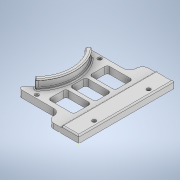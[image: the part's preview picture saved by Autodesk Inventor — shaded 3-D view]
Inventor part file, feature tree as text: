
AUTODESK INVENTOR PART (.ipt)
format: ipt  version: 2022 (Build 260153000, 153)  size: 4,516,864 bytes
history: native  units: in
note: dims shown in document units (in); Inventor stores cm internally (conversion verified against a paired STEP export)
features: sketch x19, extrude x13, fillet x9, hole x2, sweep x2, plane x1, mirror x1, chamfer x1
ambient origin geometry x8: Origin, YZ Plane, XZ Plane, XY Plane, X Axis, Y Axis, Z Axis, Center Point
bodies: Solid1 (feature_tree)
feature tree (48):
  extrude  "Extrusion1"  Depth=2.9685in
  sketch  "Sketch3"  dims[d2=0.1575in d3=0.0in d5=1.7008in d15=0.1181in]
  extrude  "Extrusion2"  Depth=0.1181in
  plane  "Work Plane1"
  fillet  "Fillet1"  Radius=0.1181in
  mirror  "Mirror1"
  extrude  "Extrusion4"  Depth=0.1181in
  extrude  "Extrusion5"  Depth=0.1575in
  hole  "Hole2"  [1 undecoded]
  fillet  "Fillet2"  Radius=0.1181in
  extrude  "Extrusion8"  Depth=0.1102in
  fillet  "Fillet7"  Radius=0.2992in
  extrude  "Extrusion9"  Depth=0.5512in
  extrude  "Extrusion10"  Depth=0.0787in
  extrude  "Extrusion15"  Depth=0.3937in
  sketch  "Sketch24"  dims[d44=0.1181in d45=0.2362in d46=0.1575in d47=0.0787in d48=90.0deg d49=0.315in d50=0.8108in d51=0.0394in]
  fillet  "Fillet17"  Radius=0.3937in
  sketch  "Sketch27"  dims[d85=1.2598in d86=1.4843in d89=0.3937in d90=0.0in]
  sweep  "Sweep7"
  sweep  "Sweep9"
  hole  "Hole4"  [1 undecoded]
  chamfer  "Chamfer2"  Distance=0.2953in
  extrude  "Extrusion18"  Depth=0.0787in
  fillet  "Fillet25"  Radius=0.2008in
  extrude  "Extrusion19"  Depth=0.0787in
  fillet  "Fillet26"  Radius=0.0315in
  sketch  "Sketch34"  dims[d188=2.5433in]
  extrude  "Extrusion20"  TaperAngle=0.0deg  [1 undecoded]
  fillet  "Fillet27"  Radius=0.6339in
  extrude  "Extrusion21"  Depth=0.0787in
  fillet  "Fillet29"  Radius=0.1575in
  extrude  "Extrusion22"  Depth=0.0787in
  fillet  "Fillet30"  Radius=0.2008in
  sketch  "Sketch2"  dims[d0=1.6142in d1=2.9685in]
  sketch  "Sketch4"  dims[d16=0.1181in d18=0.1457in]
  sketch  "Sketch7"  dims[d19=0.1575in d20=0.1575in]
  sketch  "Sketch10"  dims[d21=0.0984in d22=0.7874in d24=2.5669in d25=0.3937in d27=0.3937in d29=0.1181in d30=0.0in]
  sketch  "Sketch11"  dims[d36=0.0394in d37=0.1102in d38=0.2992in]
  sketch  "Sketch12"  dims[d39=0.0591in d40=0.0in d41=0.5512in]
  sketch  "Sketch23"  dims[d42=0.0591in d43=0.0in]
  sketch  "3D Sketch7"
  sketch  "Sketch29"  dims[d91=0.0787in d93=1.0236in]
  sketch  "3D Sketch9"
  sketch  "Sketch31"  dims[d95=0.4016in d96=0.0in d97=1.0236in]
  sketch  "Sketch32"  dims[d99=0.4016in d100=0.0in d167=2.2677in]
  sketch  "Sketch33"  dims[d168=2.1654in]
  sketch  "Sketch35"  dims[d189=1.5748in]
  sketch  "Sketch37"  dims[d190=0.3022in d191=0.2953in d192=0.0in d193=0.0394in d194=0.2008in d195=0.0374in d200=0.0315in d218=0.0in d219=0.0in d222=0.6339in d223=0.6339in d224=0.1575in d229=0.0433in d230=0.2008in d231=0.0374in d232=0.0in d233=0.0in d234=0.098in d245=0.379in d248=0.379in d249=0.1018in d250=0.0866in d251=0.2362in d252=0.1575in d253=0.0787in d254=90.0deg d255=0.315in d256=0.8108in d257=0.0197in d258=0.0787in d259=45.0deg d260=0.1018in d269=0.1181in d270=0.0in d273=2.4252in d274=0.0394in d278=0.3937in d279=0.0in d280=0.1181in d283=0.9409in d285=0.1181in d286=0.9409in d288=0.4016in d289=0.4016in d290=0.1575in d291=0.3937in d292=0.0in d293=0.1969in d296=0.2559in d297=0.9409in d298=0.9409in d299=0.1575in d300=0.0in d301=0.0787in d302=1.8504in d303=0.7244in d304=0.5591in d305=0.7976in d306=0.1181in d307=0.1181in d308=0.5577in d309=0.4987in d310=0.3937in d311=0.0in d312=0.0787in d52=0.8108in d53=0.0025in d54=0.0295in d55=0.0148in d140=0.0in d141=0.0in d142=0.0in d143=0.0in d144=0.0344in d237=0.0in d238=0.0in d239=0.0in d240=0.0in]
note: 3 required parameter values undecoded (feature->parameter linkage not recoverable at this tier; creation-order binding heuristic only, values carry confidence <= 0.55)
